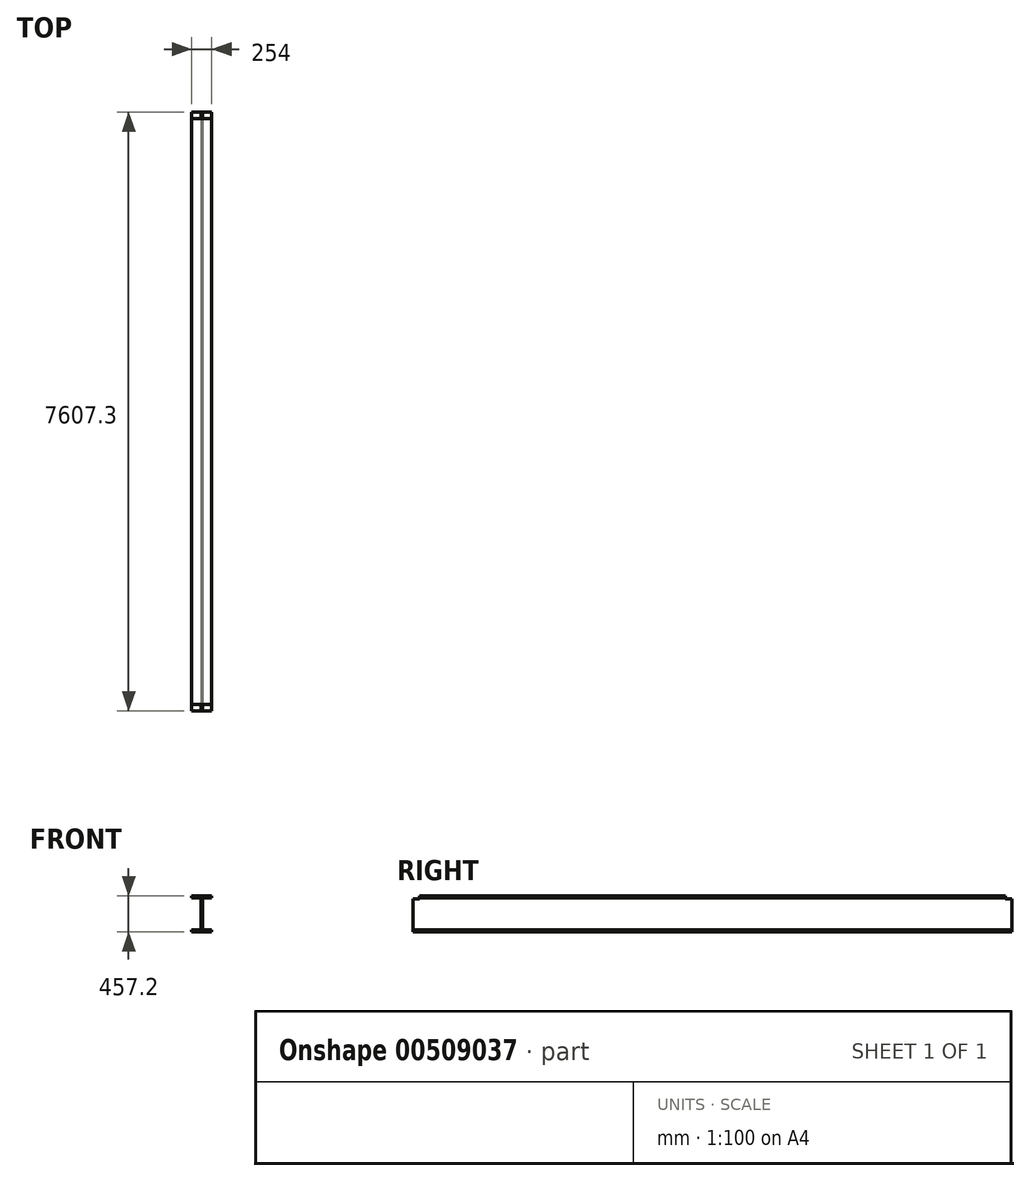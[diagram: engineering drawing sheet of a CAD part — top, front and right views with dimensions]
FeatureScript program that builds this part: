
annotation { "Feature Type Name" : "Feature", "Feature Type Description" : "" }
export const myFeature = defineFeature(function(context is Context, id is Id, definition is map)
    precondition{}
    {
        {
            var Q0;
            Q0=qCreatedBy(makeId("Front.planeOp"),FACE);
            var sketch = newSketch(context, id + "F0", { "sketchPlane" : qUnion([Q0])});
            skLineSegment(sketch, "E0", {"start": v(127, -203.2) * mm, "end": v(12.06, -203.2) * mm});
            skLineSegment(sketch, "E1", {"start": v(9.52, -200.66) * mm, "end": v(9.52, 200.66) * mm});
            skLineSegment(sketch, "E2", {"start": v(12.06, 203.2) * mm, "end": v(127, 203.2) * mm});
            skLineSegment(sketch, "E3", {"start": v(-127, 203.2) * mm, "end": v(-12.06, 203.2) * mm});
            skLineSegment(sketch, "E4", {"start": v(-9.53, 200.66) * mm, "end": v(-9.53, -200.66) * mm});
            skLineSegment(sketch, "E5", {"start": v(-12.06, -203.2) * mm, "end": v(-127, -203.2) * mm});
            skLineSegment(sketch, "E6", {"start": v(0, 0) * mm, "end": v(-9.52, 0) * mm, "construction": true});
            skLineSegment(sketch, "E7", {"start": v(0, 0) * mm, "end": v(9.52, 0) * mm, "construction": true});
            skLineSegment(sketch, "E8", {"start": v(0, 0) * mm, "end": v(0, 228.6) * mm, "construction": true});
            skLineSegment(sketch, "E9", {"start": v(0, 0) * mm, "end": v(0, -228.6) * mm, "construction": true});
            skPoint(sketch, "E10.visualSharp", {"position": v(-9.53, 203.2) * mm});
            skArc(sketch, "E10.filletArc", {"start": v(-9.52, 200.66) * mm, "mid": v(-10.27, 202.46) * mm, "end": v(-12.06, 203.2) * mm});
            skPoint(sketch, "E11.visualSharp", {"position": v(9.53, 203.2) * mm});
            skArc(sketch, "E11.filletArc", {"start": v(12.06, 203.2) * mm, "mid": v(10.27, 202.46) * mm, "end": v(9.52, 200.66) * mm});
            skPoint(sketch, "E12.visualSharp", {"position": v(9.53, -203.2) * mm});
            skArc(sketch, "E12.filletArc", {"start": v(9.52, -200.66) * mm, "mid": v(10.27, -202.46) * mm, "end": v(12.06, -203.2) * mm});
            skPoint(sketch, "E13.visualSharp", {"position": v(-9.53, -203.2) * mm});
            skArc(sketch, "E13.filletArc", {"start": v(-12.06, -203.2) * mm, "mid": v(-10.27, -202.46) * mm, "end": v(-9.52, -200.66) * mm});
            skPoint(sketch, "E14.visualSharp", {"position": v(-127, 228.6) * mm});
            skPoint(sketch, "E15.visualSharp", {"position": v(127, 228.6) * mm});
            skPoint(sketch, "E16.visualSharp", {"position": v(127, 203.2) * mm});
            skPoint(sketch, "E17.visualSharp", {"position": v(127, -228.6) * mm});
            skPoint(sketch, "E18.visualSharp", {"position": v(-127, -203.2) * mm});
            skPoint(sketch, "E19.visualSharp", {"position": v(-127, -228.6) * mm});
            skLineSegment(sketch, "E20", {"start": v(127, -203.2) * mm, "end": v(127, -228.6) * mm});
            skLineSegment(sketch, "E21", {"start": v(-127, -203.2) * mm, "end": v(-127, -228.6) * mm});
            skLineSegment(sketch, "E22", {"start": v(-127, 228.6) * mm, "end": v(-127, 203.2) * mm});
            skLineSegment(sketch, "E23", {"start": v(127, 228.6) * mm, "end": v(127, 203.2) * mm});
            skLineSegment(sketch, "E24", {"start": v(-127, 228.6) * mm, "end": v(127, 228.6) * mm});
            skLineSegment(sketch, "E25", {"start": v(-127, -228.6) * mm, "end": v(127, -228.6) * mm});
            skSolve(sketch);
        }
        {
            var Q0;
            Q0=makeQuery(id+"F0.imprint","IMPRINT",FACE,{"disambiguationData":[TD([[makeQuery(id+"F0.imprint","IMPRINT",EDGE,{"derivedFrom":sQuery(id+"F0.wireOp",EDGE,"E0")}),1.0]])]});
            extrude(context, id + "F1", {"entities" : qUnion([Q0]), "oppositeDirection" : true, "depth" : 7607.3 * mm, "offsetDistance" : 25.4 * mm});
        }
        {
            var Q0;
            Q0=makeQuery(id+"F1.opExtrude","SWEPT_FACE",FACE,{"disambiguationData":[OSD([sQuery(id+"F0.wireOp",EDGE,"E22")])]});
            var sketch = newSketch(context, id + "F2", { "sketchPlane" : qUnion([Q0])});
            skLineSegment(sketch, "E26.bottom", {"start": v(-7607.3, 228.6) * mm, "end": v(-7524.75, 228.6) * mm});
            skLineSegment(sketch, "E26.top", {"start": v(-7607.3, 190.5) * mm, "end": v(-7524.75, 190.5) * mm});
            skLineSegment(sketch, "E26.left", {"start": v(-7607.3, 228.6) * mm, "end": v(-7607.3, 190.5) * mm});
            skLineSegment(sketch, "E26.right", {"start": v(-7524.75, 228.6) * mm, "end": v(-7524.75, 190.5) * mm});
            skSolve(sketch);
        }
        {
            var Q0;
            {var subQ0=sQuery(id+"F2.wireOp",EDGE,"E26.bottom");Q0=makeQuery(id+"F2.imprint","IMPRINT",FACE,{"disambiguationData":[TD([[makeQuery(id+"F2.imprint","IMPRINT",EDGE,{"derivedFrom":subQ0}),-1.0]])]});}
            var Q1;
            {var subQ0=sQuery(id+"F2.wireOp",EDGE,"E26.top");Q1=makeQuery(id+"F2.imprint","IMPRINT",FACE,{"disambiguationData":[TD([[makeQuery(id+"F2.imprint","IMPRINT",EDGE,{"derivedFrom":subQ0}),1.0]])]});}
            extrude(context, id + "F3", {"entities" : qUnion([Q0, Q1]), "operationType" : NewBodyOperationType.REMOVE, "endBound" : BoundingType.THROUGH_ALL, "oppositeDirection" : true, "depth" : 25.4 * mm});
        }
        {
            var Q0;
            Q0=makeQuery(id+"F1.opExtrude","SWEPT_FACE",FACE,{"disambiguationData":[OSD([sQuery(id+"F0.wireOp",EDGE,"E22")])]});
            var sketch = newSketch(context, id + "F4", { "sketchPlane" : qUnion([Q0])});
            skLineSegment(sketch, "E27.bottom", {"start": v(0, 228.6) * mm, "end": v(-82.55, 228.6) * mm});
            skLineSegment(sketch, "E27.top", {"start": v(0, 190.5) * mm, "end": v(-82.55, 190.5) * mm});
            skLineSegment(sketch, "E27.left", {"start": v(0, 228.6) * mm, "end": v(0, 190.5) * mm});
            skLineSegment(sketch, "E28", {"start": v(-82.55, 228.6) * mm, "end": v(-82.55, 190.5) * mm});
            skSolve(sketch);
        }
        {
            var Q0;
            {var subQ0=sQuery(id+"F4.wireOp",EDGE,"E27.bottom");Q0=makeQuery(id+"F4.imprint","IMPRINT",FACE,{"disambiguationData":[TD([[makeQuery(id+"F4.imprint","IMPRINT",EDGE,{"derivedFrom":subQ0}),-1.0]])]});}
            var Q1;
            {var subQ0=sQuery(id+"F4.wireOp",EDGE,"E27.top");Q1=makeQuery(id+"F4.imprint","IMPRINT",FACE,{"disambiguationData":[TD([[makeQuery(id+"F4.imprint","IMPRINT",EDGE,{"derivedFrom":subQ0}),-1.0]])]});}
            extrude(context, id + "F5", {"entities" : qUnion([Q0, Q1]), "operationType" : NewBodyOperationType.REMOVE, "endBound" : BoundingType.THROUGH_ALL, "oppositeDirection" : true, "depth" : 25.4 * mm});
        }
    });
